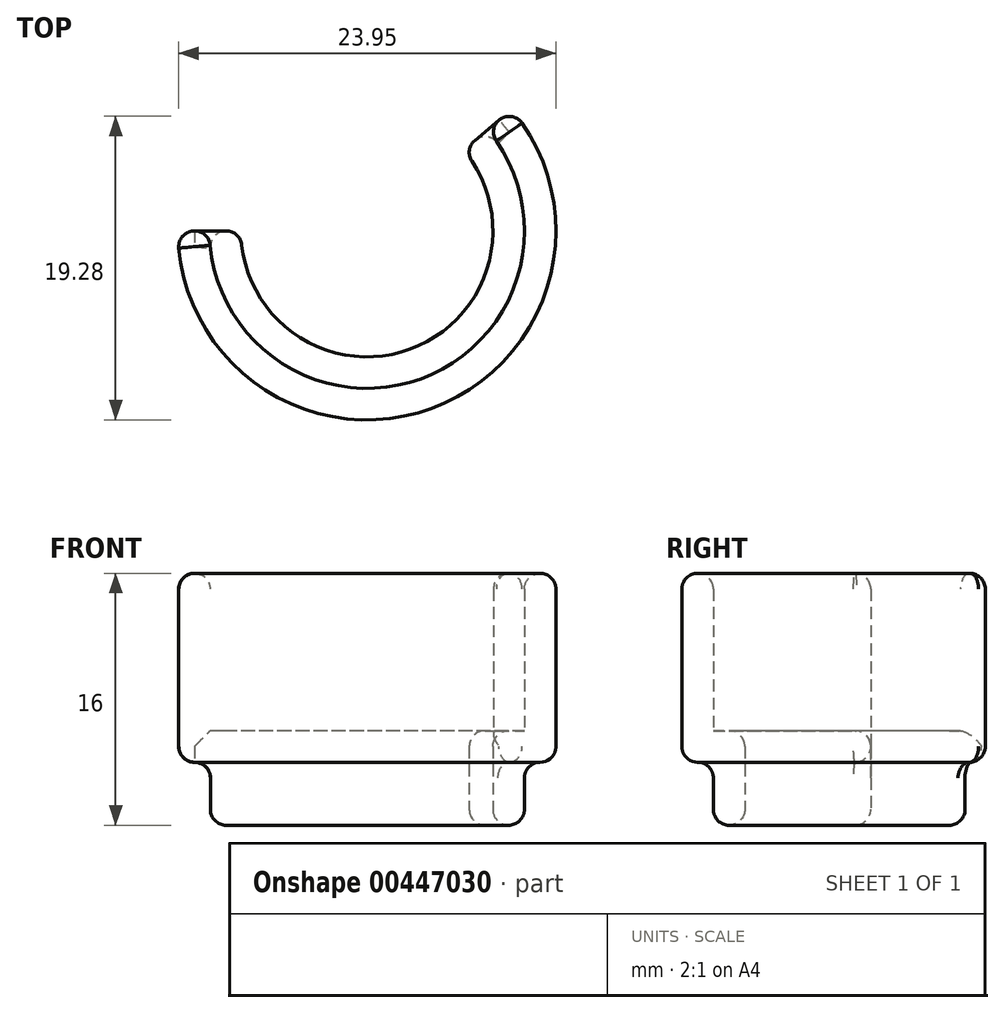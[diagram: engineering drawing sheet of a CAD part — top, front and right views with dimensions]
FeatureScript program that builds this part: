
annotation { "Feature Type Name" : "Feature", "Feature Type Description" : "" }
export const myFeature = defineFeature(function(context is Context, id is Id, definition is map)
    precondition{}
    {
        {
            var Q0;
            Q0=qCreatedBy(makeId("Front.planeOp"),FACE);
            var sketch = newSketch(context, id + "F0", { "sketchPlane" : qUnion([Q0])});
            skLineSegment(sketch, "E0", {"start": v(-8, 1) * mm, "end": v(-8, 5) * mm});
            skLineSegment(sketch, "E1", {"start": v(-9, 6) * mm, "end": v(-10, 6) * mm});
            skLineSegment(sketch, "E2", {"start": v(-10, 6) * mm, "end": v(-10, 15) * mm});
            skLineSegment(sketch, "E3", {"start": v(-11, 16) * mm, "end": v(-11, 16) * mm});
            skLineSegment(sketch, "E4", {"start": v(-12, 15) * mm, "end": v(-12, 5) * mm});
            skLineSegment(sketch, "E5", {"start": v(-11, 4) * mm, "end": v(-11, 4) * mm});
            skLineSegment(sketch, "E6", {"start": v(-10, 3) * mm, "end": v(-10, 1) * mm});
            skLineSegment(sketch, "E7", {"start": v(-9, 0) * mm, "end": v(-9, 0) * mm});
            skPoint(sketch, "E8.visualSharp", {"position": v(-10, 4) * mm});
            skArc(sketch, "E8.filletArc", {"start": v(-10, 3) * mm, "mid": v(-10.3, 3.7) * mm, "end": v(-11, 4) * mm});
            skPoint(sketch, "E9.visualSharp", {"position": v(-12, 4) * mm});
            skArc(sketch, "E9.filletArc", {"start": v(-12, 5) * mm, "mid": v(-11.7, 4.3) * mm, "end": v(-11, 4) * mm});
            skPoint(sketch, "E10.visualSharp", {"position": v(-12, 16) * mm});
            skArc(sketch, "E10.filletArc", {"start": v(-11, 16) * mm, "mid": v(-11.7, 15.7) * mm, "end": v(-12, 15) * mm});
            skPoint(sketch, "E11.visualSharp", {"position": v(-10, 0) * mm});
            skArc(sketch, "E11.filletArc", {"start": v(-10, 1) * mm, "mid": v(-9.7, 0.3) * mm, "end": v(-9, 0) * mm});
            skLineSegment(sketch, "E12", {"start": v(0, 0) * mm, "end": v(0, 17.73) * mm, "construction": true});
            skPoint(sketch, "E13.visualSharp", {"position": v(-8, 6) * mm});
            skArc(sketch, "E13.filletArc", {"start": v(-8, 5) * mm, "mid": v(-8.3, 5.7) * mm, "end": v(-9, 6) * mm});
            skPoint(sketch, "E14.visualSharp", {"position": v(-10, 16) * mm});
            skArc(sketch, "E14.filletArc", {"start": v(-10, 15) * mm, "mid": v(-10.3, 15.7) * mm, "end": v(-11, 16) * mm});
            skPoint(sketch, "E15.visualSharp", {"position": v(-8, 0) * mm});
            skArc(sketch, "E15.filletArc", {"start": v(-9, 0) * mm, "mid": v(-8.3, 0.3) * mm, "end": v(-8, 1) * mm});
            skSolve(sketch);
        }
        {
            var Q0;
            Q0=makeQuery(id+"F0.imprint","IMPRINT",FACE,{"disambiguationData":[TD([[makeQuery(id+"F0.imprint","IMPRINT",EDGE,{"derivedFrom":sQuery(id+"F0.wireOp",EDGE,"E0")}),1.0]])]});
            var Q1;
            Q1=sQuery(id+"F0.wireOp",EDGE,"E12");
            revolve(context, id + "F1", {"entities" : qUnion([Q0]), "axis" : qUnion([Q1]), "revolveType" : RevolveType.ONE_DIRECTION, "angle" : 220 * degree});
        }
        {
            var Q0;
            Q0=makeQuery(id+"F1.opRevolve","CAP_EDGE",EDGE,{"disambiguationData":[OSD([sQuery(id+"F0.wireOp",EDGE,"E2")])],"isStart":false});
            var Q1;
            Q1=makeQuery(id+"F1.opRevolve","CAP_EDGE",EDGE,{"disambiguationData":[OSD([sQuery(id+"F0.wireOp",EDGE,"E1")])],"isStart":false});
            var Q2;
            Q2=makeQuery(id+"F1.opRevolve","CAP_EDGE",EDGE,{"disambiguationData":[OSD([sQuery(id+"F0.wireOp",EDGE,"E0")])],"isStart":false});
            var Q3;
            Q3=makeQuery(id+"F1.opRevolve","CAP_EDGE",EDGE,{"disambiguationData":[OSD([sQuery(id+"F0.wireOp",EDGE,"E4")])],"isStart":false});
            var Q4;
            Q4=makeQuery(id+"F1.opRevolve","CAP_EDGE",EDGE,{"disambiguationData":[OSD([sQuery(id+"F0.wireOp",EDGE,"E10.filletArc")])],"isStart":false});
            var Q5;
            Q5=makeQuery(id+"F1.opRevolve","CAP_EDGE",EDGE,{"disambiguationData":[OSD([sQuery(id+"F0.wireOp",EDGE,"E3")])],"isStart":false});
            var Q6;
            Q6=makeQuery(id+"F1.opRevolve","CAP_EDGE",EDGE,{"disambiguationData":[OSD([sQuery(id+"F0.wireOp",EDGE,"E9.filletArc")])],"isStart":false});
            var Q7;
            Q7=makeQuery(id+"F1.opRevolve","CAP_EDGE",EDGE,{"disambiguationData":[OSD([sQuery(id+"F0.wireOp",EDGE,"E8.filletArc")])],"isStart":false});
            var Q8;
            Q8=makeQuery(id+"F1.opRevolve","CAP_EDGE",EDGE,{"disambiguationData":[OSD([sQuery(id+"F0.wireOp",EDGE,"E6")])],"isStart":false});
            var Q9;
            Q9=makeQuery(id+"F1.opRevolve","CAP_EDGE",EDGE,{"disambiguationData":[OSD([sQuery(id+"F0.wireOp",EDGE,"E11.filletArc")])],"isStart":false});
            var Q10;
            Q10=makeQuery(id+"F1.opRevolve","CAP_EDGE",EDGE,{"disambiguationData":[OSD([sQuery(id+"F0.wireOp",EDGE,"E4")])],"isStart":true});
            var Q11;
            Q11=makeQuery(id+"F1.opRevolve","CAP_EDGE",EDGE,{"disambiguationData":[OSD([sQuery(id+"F0.wireOp",EDGE,"E10.filletArc")])],"isStart":true});
            var Q12;
            Q12=makeQuery(id+"F1.opRevolve","CAP_EDGE",EDGE,{"disambiguationData":[OSD([sQuery(id+"F0.wireOp",EDGE,"E2")])],"isStart":true});
            var Q13;
            Q13=makeQuery(id+"F1.opRevolve","CAP_EDGE",EDGE,{"disambiguationData":[OSD([sQuery(id+"F0.wireOp",EDGE,"E1")])],"isStart":true});
            var Q14;
            Q14=makeQuery(id+"F1.opRevolve","CAP_EDGE",EDGE,{"disambiguationData":[OSD([sQuery(id+"F0.wireOp",EDGE,"E0")])],"isStart":true});
            var Q15;
            Q15=makeQuery(id+"F1.opRevolve","CAP_EDGE",EDGE,{"disambiguationData":[OSD([sQuery(id+"F0.wireOp",EDGE,"E7")])],"isStart":true});
            var Q16;
            Q16=makeQuery(id+"F1.opRevolve","CAP_EDGE",EDGE,{"disambiguationData":[OSD([sQuery(id+"F0.wireOp",EDGE,"E11.filletArc")])],"isStart":true});
            var Q17;
            Q17=makeQuery(id+"F1.opRevolve","CAP_EDGE",EDGE,{"disambiguationData":[OSD([sQuery(id+"F0.wireOp",EDGE,"E6")])],"isStart":true});
            var Q18;
            Q18=makeQuery(id+"F1.opRevolve","CAP_EDGE",EDGE,{"disambiguationData":[OSD([sQuery(id+"F0.wireOp",EDGE,"E8.filletArc")])],"isStart":true});
            var Q19;
            Q19=makeQuery(id+"F1.opRevolve","CAP_EDGE",EDGE,{"disambiguationData":[OSD([sQuery(id+"F0.wireOp",EDGE,"E9.filletArc")])],"isStart":true});
            fillet(context, id + "F2", {"entities" : qUnion([Q0, Q1, Q2, Q3, Q4, Q5, Q6, Q7, Q8, Q9, Q10, Q11, Q12, Q13, Q14, Q15, Q16, Q17, Q18, Q19]), "radius" : 1 * mm, "tangentPropagation" : true, "allowEdgeOverflow" : false});
        }
    });
